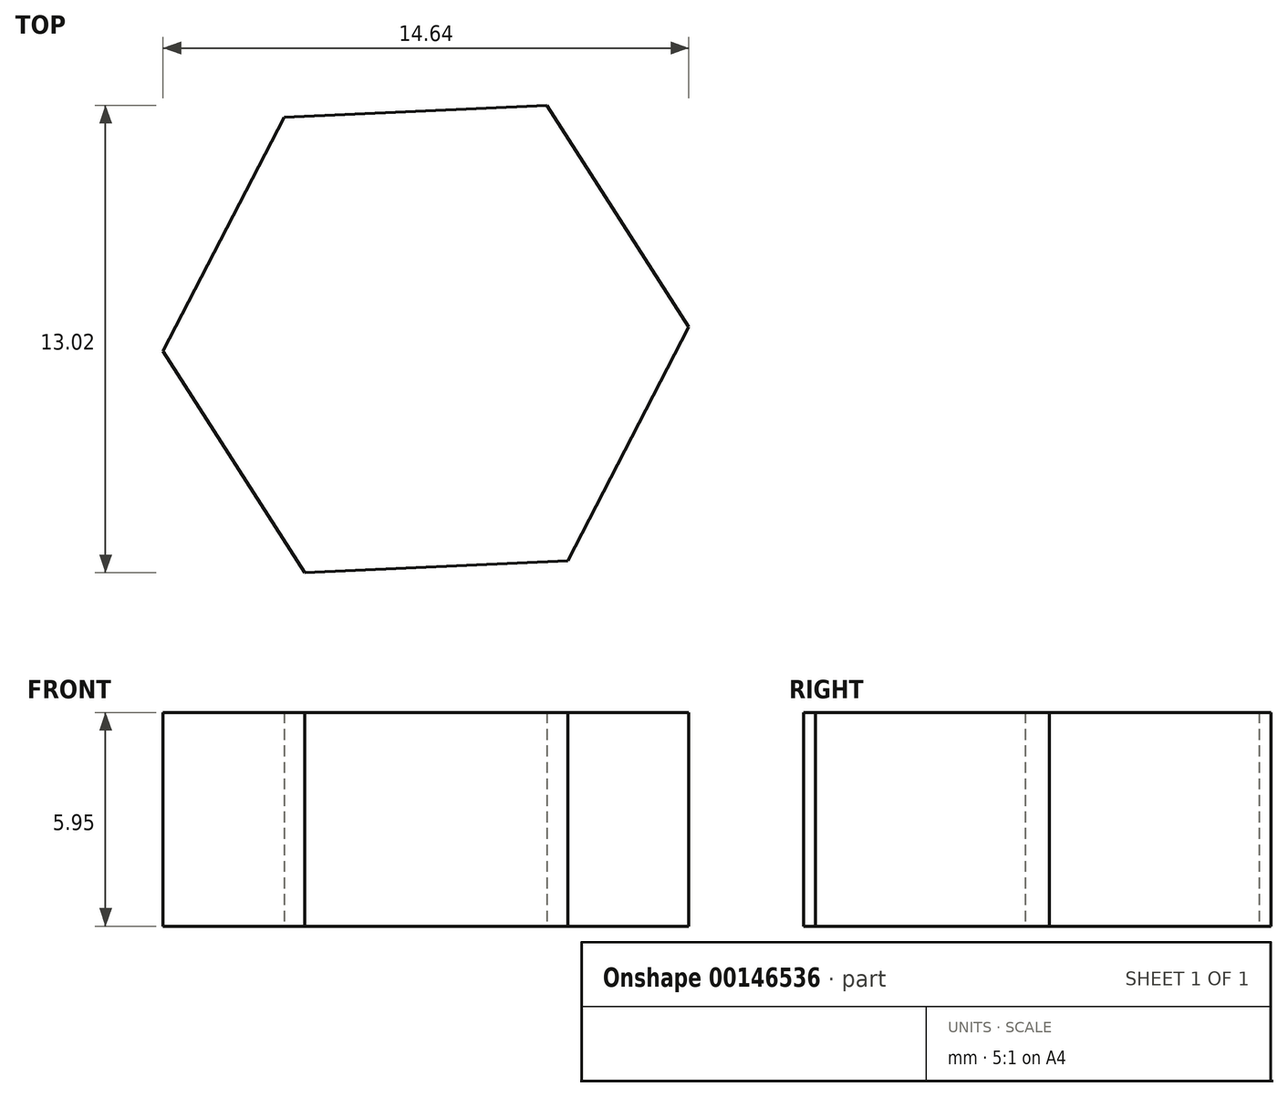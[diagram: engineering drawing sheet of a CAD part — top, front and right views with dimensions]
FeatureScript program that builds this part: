
annotation { "Feature Type Name" : "Feature", "Feature Type Description" : "" }
export const myFeature = defineFeature(function(context is Context, id is Id, definition is map)
    precondition{}
    {
        {
            var Q0;
            Q0=qCreatedBy(makeId("Top.planeOp"),FACE);
            var sketch = newSketch(context, id + "F0", { "sketchPlane" : qUnion([Q0])});
            skCircle(sketch, "E0.cCircle", {"center": v(0, 0) * mm, "radius": 6.35 * mm, "construction": true});
            skLineSegment(sketch, "E0.0", {"start": v(7.32, 0.33) * mm, "end": v(3.95, -6.18) * mm});
            skLineSegment(sketch, "E0.1", {"start": v(3.95, -6.18) * mm, "end": v(-3.37, -6.5) * mm});
            skLineSegment(sketch, "E0.2", {"start": v(-3.37, -6.5) * mm, "end": v(-7.32, -0.33) * mm});
            skLineSegment(sketch, "E0.3", {"start": v(-7.32, -0.33) * mm, "end": v(-3.95, 6.18) * mm});
            skLineSegment(sketch, "E0.4", {"start": v(-3.95, 6.18) * mm, "end": v(3.37, 6.5) * mm});
            skLineSegment(sketch, "E0.5", {"start": v(3.37, 6.5) * mm, "end": v(7.32, 0.33) * mm});
            skPoint(sketch, "E0.0.midPoint", {"position": v(5.64, -2.92) * mm});
            skSolve(sketch);
        }
        {
            var Q0;
            Q0=qSketchRegion(id+"F0",true);
            extrude(context, id + "F1", {"entities" : qUnion([Q0]), "depth" : 5.95 * mm});
        }
    });
